# Revit family: ITK_Органайзер-хомут вертикальный_42U_ 70x12мм_Серый
name_source: partatom
category: Обобщенные модели
units: mm (PartAtom-declared; Revit-internal decimal feet)

## family parameters
Всегда вертикально = Да
Может служить основой для арматурных стержней = Нет
На основе рабочей плоскости = Нет
Общий = Нет
При загрузке вырезать с полостями = Нет
Размер круглого соединителя = Использовать диаметр
Тип детали = Нормальный
Точка расчета площади = Нет

## types (1)
- CM35-070-42U-Z
    ADSK_URL страницы изделия = https://www.itk-group.ru
    ADSK_Версия Revit = 2019
    ADSK_Версия семейства = 1.0
    ADSK_Группирование = I. ЩИТЫ И ПУЛЬТЫ
    ADSK_Единица измерения = шт
    ADSK_Завод-изготовитель = IEK
    ADSK_Код изделия = CM35-070-42U-Z
    ADSK_Масса = 1.5
    ADSK_Материал наименование = Листовая сталь
    ADSK_Наименование = ITK Органайзер-хомут вертикальный 42U 70x12мм с крепежом сер
    IEK_URL = https://www.itk-group.ru
    IEK_Описание = Широкий ассортимент видов и исполнений.
Совместимы со всеми 19" шкафами и стойками ITK.
Современный привлекательный дизайн и продуманная конструкция.
Удобны в монтаже и эксплуатации.
Соответствие российским и международным стандартам.
Обеспечивают эффективное использование монтажного пространства шкафа.
Все органайзеры идут с крепежом.
Поставляются в качественной компактной упаковке.
    IEK_Цена за единицу = 1248.64
    KSI_CMa_Строительные материалы = 10.03.02.06
    KSI_CPr_Строительные изделия = 61.1.04.08
    URL = https://www.iek.ru
    Высота = 1867 мм
    Глубина = 12 мм
    Изготовитель = ITK
    Материал = Окраска - RAL 7035
    Тип монтажа = Установка на захваты
    Ширина = 70 мм
